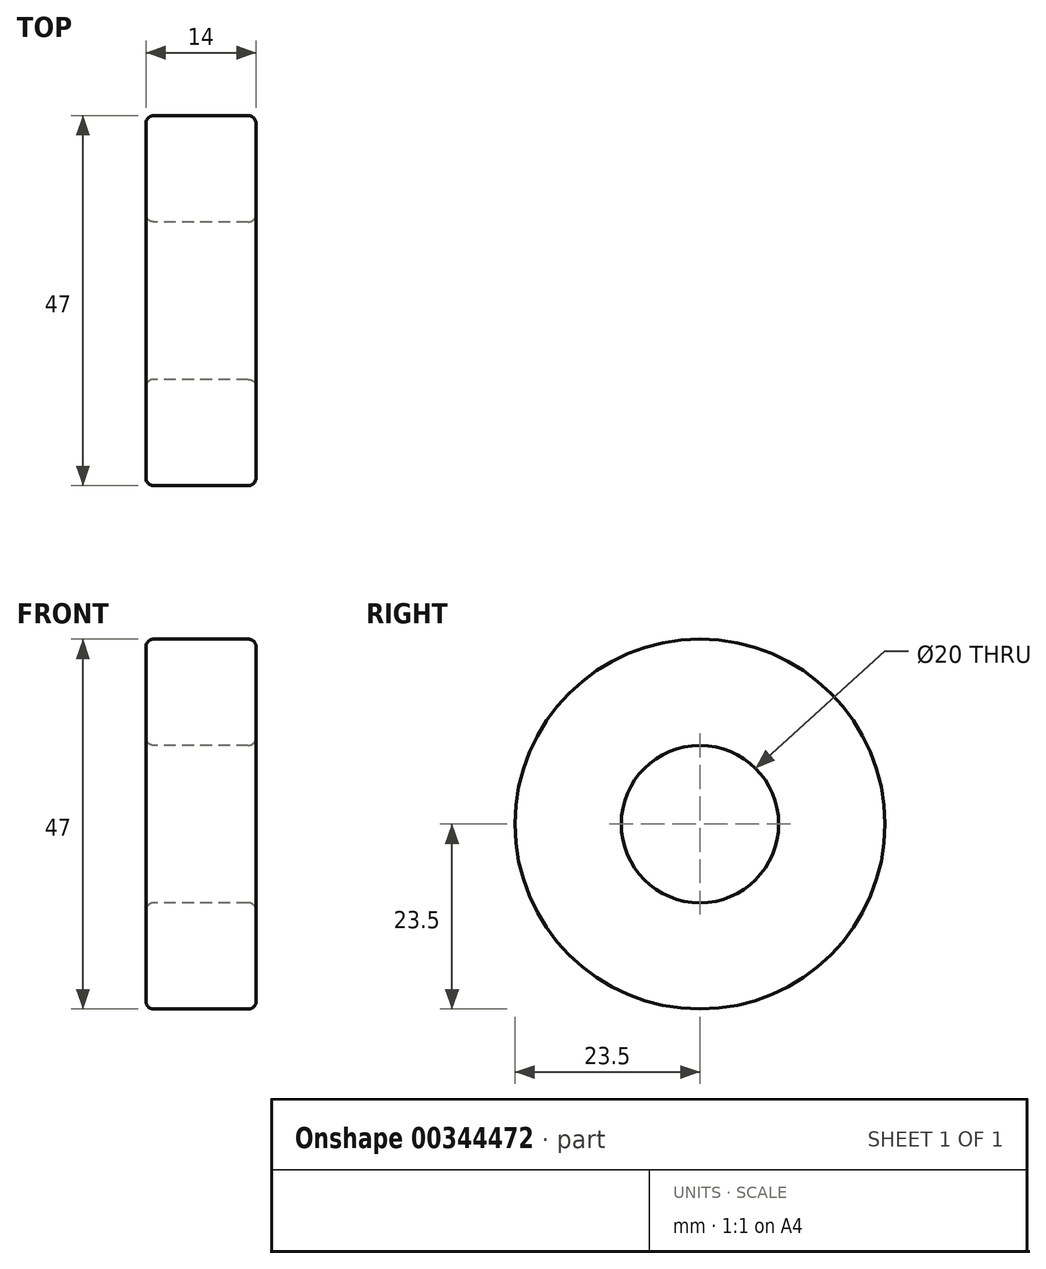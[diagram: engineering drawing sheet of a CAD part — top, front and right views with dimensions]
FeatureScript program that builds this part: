
annotation { "Feature Type Name" : "Feature", "Feature Type Description" : "" }
export const myFeature = defineFeature(function(context is Context, id is Id, definition is map)
    precondition{}
    {
        {
            var Q0;
            Q0=qCreatedBy(makeId("Right.planeOp"),FACE);
            var sketch = newSketch(context, id + "F0", { "sketchPlane" : qUnion([Q0])});
            skCircle(sketch, "E0", {"center": v(0, 0) * mm, "radius": 10 * mm});
            skCircle(sketch, "E1", {"center": v(0, 0) * mm, "radius": 23.5 * mm});
            skSolve(sketch);
        }
        {
            var Q0;
            Q0 = qSketchRegion(id + "F0", true);
            extrude(context, id + "F1", {"entities" : qUnion([Q0]), "endBound" : BoundingType.SYMMETRIC, "depth" : 14 * mm});
        }
        {
            var Q0;
            Q0=makeQuery(id+"F1.opExtrude","CAP_FACE",FACE,{"disambiguationData":[OSD([sQuery(id+"F0.wireOp",EDGE,"E0"),sQuery(id+"F0.wireOp",EDGE,"E1")])],"isStart":false});
            var Q1;
            Q1=makeQuery(id+"F1.opExtrude","CAP_FACE",FACE,{"disambiguationData":[OSD([sQuery(id+"F0.wireOp",EDGE,"E0"),sQuery(id+"F0.wireOp",EDGE,"E1")])],"isStart":true});
            fillet(context, id + "F2", {"entities" : qUnion([Q0, Q1]), "radius" : 1 * mm, "tangentPropagation" : true, "allowEdgeOverflow" : false});
        }
    });
